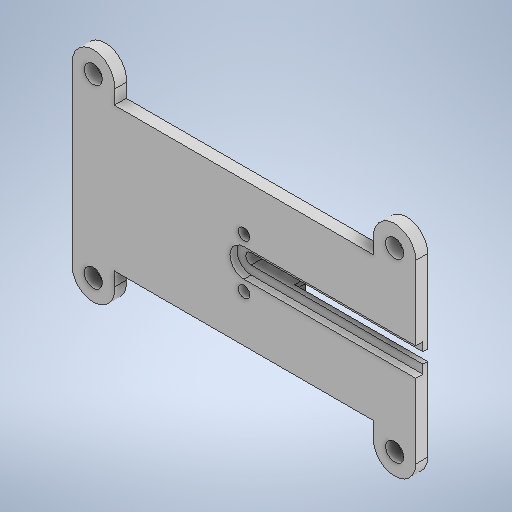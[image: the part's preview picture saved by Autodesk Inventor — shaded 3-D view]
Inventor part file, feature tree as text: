
AUTODESK INVENTOR PART (.ipt)
format: ipt  version: 2025.1 (Build 291241000, 241)  size: 325,120 bytes
history: native  units: mm
features: extrude x4, sketch x4
ambient origin geometry x8: Origin, YZ Plane, XZ Plane, XY Plane, X Axis, Y Axis, Z Axis, Center Point
bodies: Solid1 (feature_tree)
feature tree (8):
  extrude  "Extrusion1"  Depth=15.5mm
  extrude  "Extrusion2"  Depth=2.48mm
  extrude  "Extrusion3"  Depth=10.5mm
  extrude  "Extrusion4"  Depth=20.0mm
  sketch  "Sketch1"  dims[d0=2.48mm d1=15.5mm]
  sketch  "Sketch2"  dims[d2=15.5mm d3=2.48mm]
  sketch  "Sketch3"  dims[d4=10.5mm d5=10.5mm]
  sketch  "Sketch4"  dims[d6=20.0mm d7=20.0mm d8=2.65mm d9=7.25mm d10=2.8mm d11=0.0mm d12=2.5mm d13=33.2mm d14=25.0mm d15=4.9mm d16=4.2mm d17=7.3mm d18=2.75mm d19=0.0mm d20=3.25mm d21=1.65mm d22=0.0mm d25=79.5mm d26=11.75mm d27=14.25mm d28=5.1mm d29=6.6mm d30=8.8mm d31=1.5mm d32=5.1mm d33=6.6mm d34=8.8mm d35=1.5mm d36=2.3mm d37=0.0mm]
